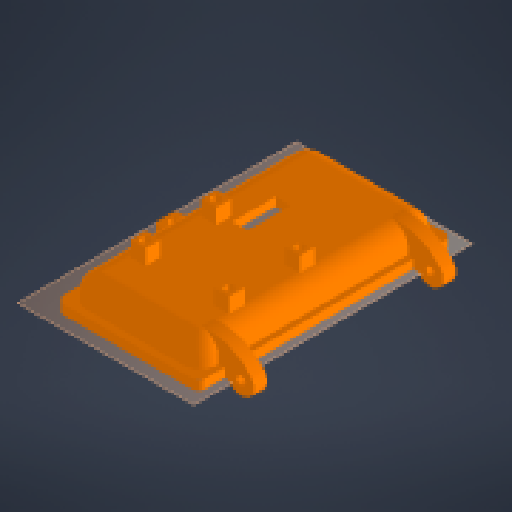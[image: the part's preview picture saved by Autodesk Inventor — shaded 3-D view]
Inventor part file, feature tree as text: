
AUTODESK INVENTOR PART (.ipt)
format: ipt  version: 2024 (Build 280153000, 153)  size: 395,776 bytes
history: native  units: mm
features: reference x32, other x15, extrude x8, sketch x8, projected_geometry x2, chamfer x1, fillet x1, shell x1, mirror x1
ambient origin geometry x8: Origin, YZ Plane, XZ Plane, XY Plane, X Axis, Y Axis, Z Axis, Center Point
bodies: Body1 (feature_tree)
feature tree (69):
  other  "Твердое тело1"
  extrude  "Выдавливание1"  Depth=2.0mm
  chamfer  "Фаска1"  Distance=3.0mm
  extrude  "Выдавливание2"  Depth=2.0mm TaperAngle=45.0deg
  other  "РабПлоскость1"
  other  "РабПлоскость2"
  extrude  "Выдавливание4"  Depth=15.5mm TaperAngle=0.0deg
  fillet  "Сопряжение1"  Radius=8.0mm
  extrude  "Выдавливание6"  Depth=45.0mm
  shell  "Оболочка1"  Thickness=95.0mm
  other  "Непосредственное редактирование2"
  other  "Непосредственное редактирование3"
  other  "РабПлоскость3"
  other  "РабПлоскость4"
  extrude  "Выдавливание10"  Depth=11.25mm TaperAngle=0.0deg
  extrude  "Выдавливание11"  Depth=8.0mm
  other  "РабПлоскость5"
  extrude  "Выдавливание13"  Depth=16.0mm TaperAngle=0.0deg
  mirror  "Зеркальное отражение5"
  other  "РабПлоскость6"
  extrude  "Выдавливание14"  Depth=4.0mm
  sketch  "Эскиз1"
  reference  "Ссылка1"
  reference  "Ссылка3"
  reference  "Ссылка4"
  reference  "Ссылка5"
  reference  "Ссылка6"
  reference  "Ссылка7"
  reference  "Ссылка8"
  reference  "Ссылка9"
  reference  "Ссылка10"
  sketch  "Эскиз2"
  reference  "Ссылка11"
  reference  "Ссылка12"
  reference  "Ссылка13"
  reference  "Ссылка14"
  reference  "Ссылка15"
  reference  "Ссылка16"
  reference  "Ссылка17"
  reference  "Ссылка18"
  reference  "Ссылка19"
  reference  "Ссылка20"
  reference  "Ссылка21"
  reference  "Ссылка22"
  sketch  "Эскиз4"
  projected_geometry  "Спроецированная петля1"
  sketch  "Эскиз6"
  projected_geometry  "Спроецированная петля2"
  sketch  "Эскиз11"
  sketch  "Эскиз12"
  reference  "Ссылка33"
  reference  "Ссылка34"
  sketch  "Эскиз14"
  reference  "Ссылка39"
  sketch  "Эскиз15"
  reference  "Ссылка40"
  reference  "Ссылка41"
  reference  "Ссылка42"
  reference  "Ссылка43"
  reference  "Ссылка44"
  reference  "Ссылка45"
  reference  "Ссылка46"
  reference  "Ссылка47"
  parser-record x1  (decoder bookkeeping rows leaked as tree rows — omitted from the tree; the rows remain in map.json)
  other  "front_box_asembly.iam"
  other  "front_box:1"
  other  "Перенос3"
  other  "Перенос4"
  other  "ts832:1"
note: 1 file-system path scrubbed to <path> (originals preserved in map.json)
